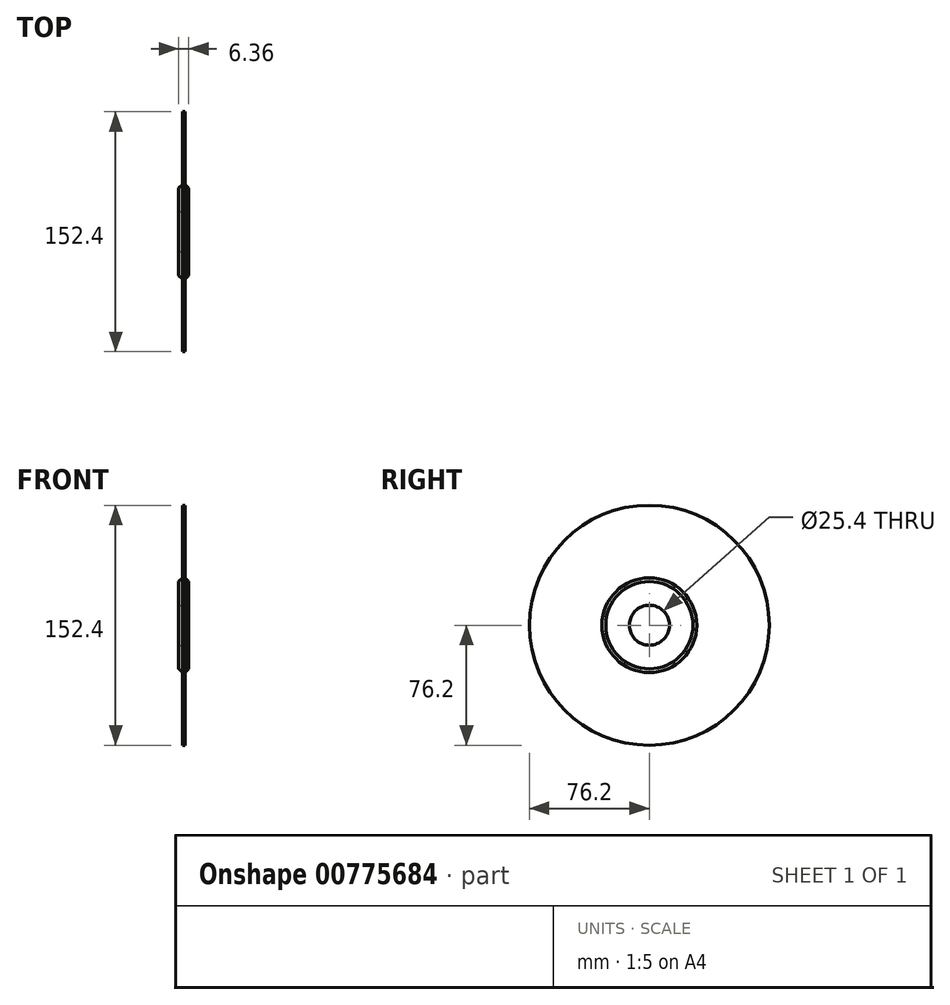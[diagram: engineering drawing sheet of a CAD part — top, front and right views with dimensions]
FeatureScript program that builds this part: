
annotation { "Feature Type Name" : "Feature", "Feature Type Description" : "" }
export const myFeature = defineFeature(function(context is Context, id is Id, definition is map)
    precondition{}
    {
        {
            var Q0;
            Q0=qCreatedBy(makeId("Front.planeOp"),FACE);
            var sketch = newSketch(context, id + "F0", { "sketchPlane" : qUnion([Q0])});
            skLineSegment(sketch, "E0", {"start": v(-3.18, 12.7) * mm, "end": v(3.17, 12.7) * mm});
            skLineSegment(sketch, "E1", {"start": v(3.17, 12.7) * mm, "end": v(3.17, 27.7) * mm});
            skLineSegment(sketch, "E2", {"start": v(3.17, 27.7) * mm, "end": v(0.8, 30.08) * mm});
            skLineSegment(sketch, "E3", {"start": v(0.8, 30.08) * mm, "end": v(0.8, 76.2) * mm});
            skLineSegment(sketch, "E4", {"start": v(0.8, 76.2) * mm, "end": v(-0.8, 76.2) * mm});
            skLineSegment(sketch, "E5", {"start": v(-0.8, 76.2) * mm, "end": v(-0.8, 30.08) * mm});
            skLineSegment(sketch, "E6", {"start": v(-0.8, 30.08) * mm, "end": v(-3.18, 27.7) * mm});
            skLineSegment(sketch, "E7", {"start": v(-3.18, 27.7) * mm, "end": v(-3.18, 12.7) * mm});
            skLineSegment(sketch, "E8", {"start": v(0, 0) * mm, "end": v(-9.7, 0) * mm});
            skSolve(sketch);
        }
        {
            var Q0;
            Q0=makeQuery(id+"F0.imprint","IMPRINT",FACE,{"disambiguationData":[TD([[makeQuery(id+"F0.imprint","IMPRINT",EDGE,{"derivedFrom":sQuery(id+"F0.wireOp",EDGE,"E0")}),1.0]])]});
            var Q1;
            Q1=sQuery(id+"F0.wireOp",EDGE,"E8");
            revolve(context, id + "F1", {"surfaceOperationType" : NewSurfaceOperationType.NEW, "entities" : qUnion([Q0]), "axis" : qUnion([Q1]), "revolveType" : RevolveType.FULL});
        }
    });
